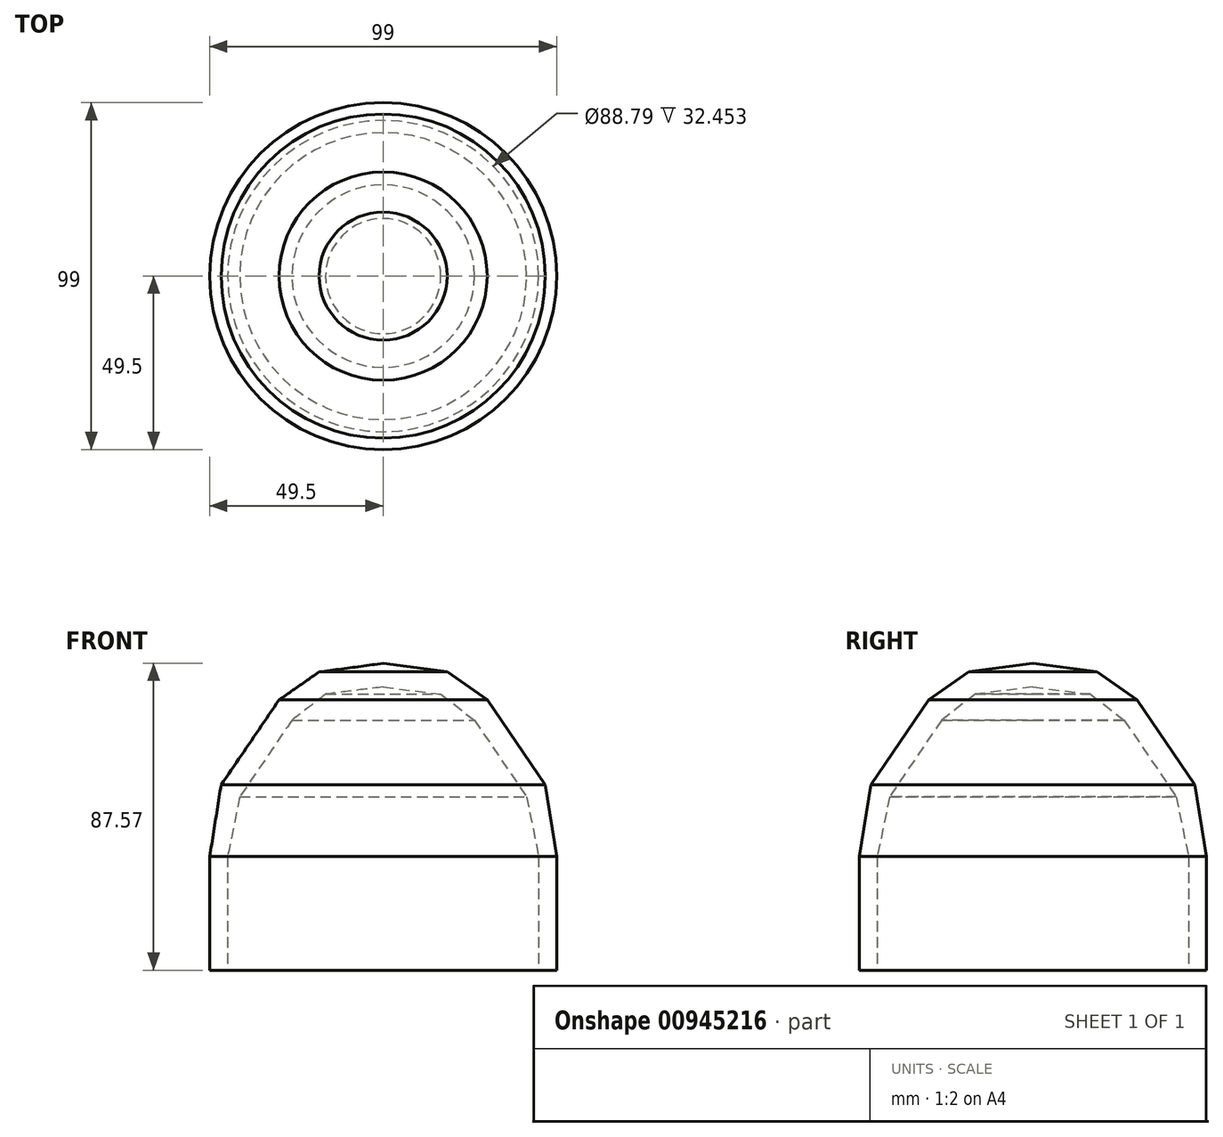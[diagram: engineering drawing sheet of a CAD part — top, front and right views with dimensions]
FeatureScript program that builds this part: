
annotation { "Feature Type Name" : "Feature", "Feature Type Description" : "" }
export const myFeature = defineFeature(function(context is Context, id is Id, definition is map)
    precondition{}
    {
        {
            var Q0;
            Q0=qCreatedBy(makeId("Right.planeOp"),FACE);
            var sketch = newSketch(context, id + "F0", { "sketchPlane" : qUnion([Q0])});
            skLineSegment(sketch, "E0", {"start": v(0, 38.07) * mm, "end": v(18.27, 35.62) * mm});
            skLineSegment(sketch, "E1", {"start": v(18.27, 35.62) * mm, "end": v(29.7, 27.66) * mm});
            skLineSegment(sketch, "E2", {"start": v(29.7, 27.66) * mm, "end": v(39.3, 13.57) * mm});
            skLineSegment(sketch, "E3", {"start": v(39.3, 13.57) * mm, "end": v(46.25, 3.36) * mm});
            skLineSegment(sketch, "E4", {"start": v(46.25, 3.36) * mm, "end": v(49.5, -17.04) * mm});
            skLineSegment(sketch, "E5", {"start": v(49.5, -17.04) * mm, "end": v(49.5, -30.72) * mm});
            skLineSegment(sketch, "E6", {"start": v(49.5, -30.72) * mm, "end": v(49.5, -49.5) * mm});
            skLineSegment(sketch, "E7", {"start": v(49.5, -49.5) * mm, "end": v(44.4, -49.5) * mm});
            skLineSegment(sketch, "E8", {"start": v(44.4, -49.5) * mm, "end": v(44.4, -30.72) * mm});
            skLineSegment(sketch, "E9", {"start": v(44.4, -30.72) * mm, "end": v(44.4, -17.04) * mm});
            skLineSegment(sketch, "E10", {"start": v(44.4, -17.04) * mm, "end": v(40.92, 0) * mm});
            skLineSegment(sketch, "E11", {"start": v(40.92, 0) * mm, "end": v(34.66, 9.2) * mm});
            skLineSegment(sketch, "E12", {"start": v(34.66, 9.2) * mm, "end": v(26.05, 21.84) * mm});
            skLineSegment(sketch, "E13", {"start": v(26.05, 21.84) * mm, "end": v(16.43, 29.29) * mm});
            skLineSegment(sketch, "E14", {"start": v(16.43, 29.29) * mm, "end": v(0, 31.33) * mm});
            skLineSegment(sketch, "E15", {"start": v(0, 31.33) * mm, "end": v(0, 38.07) * mm});
            skSolve(sketch);
        }
        {
            var Q0;
            Q0=makeQuery(id+"F0.imprint","IMPRINT",FACE,{"disambiguationData":[TD([[makeQuery(id+"F0.imprint","IMPRINT",EDGE,{"derivedFrom":sQuery(id+"F0.wireOp",EDGE,"E0")}),-1.0]])]});
            var Q1;
            Q1=sQuery(id+"F0.wireOp",EDGE,"E15");
            revolve(context, id + "F1", {"surfaceOperationType" : NewSurfaceOperationType.NEW, "entities" : qUnion([Q0]), "axis" : qUnion([Q1]), "revolveType" : RevolveType.FULL});
        }
    });
